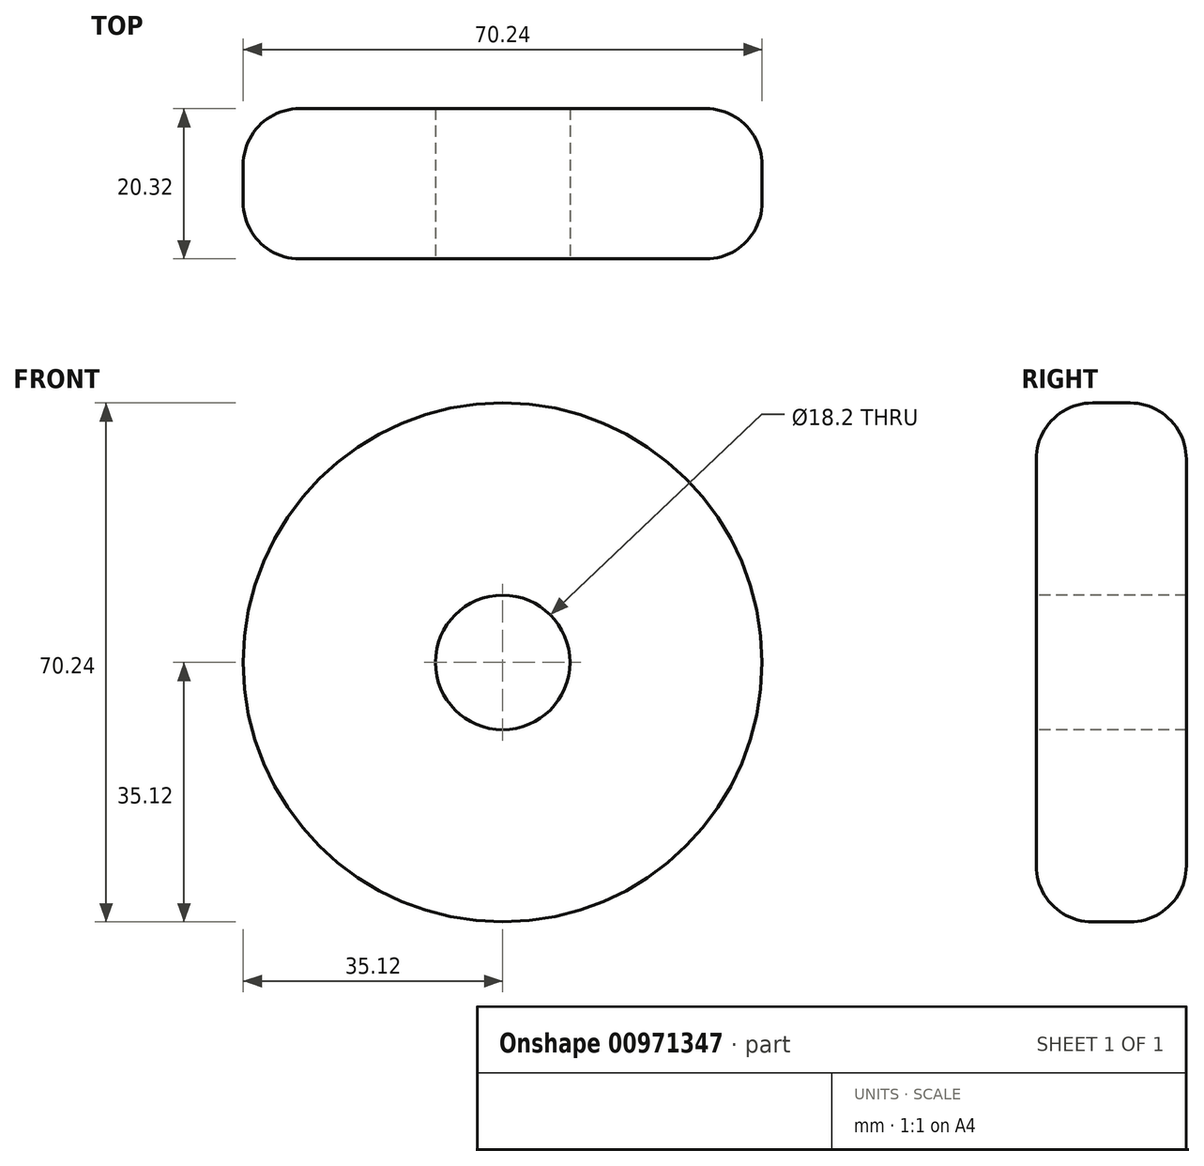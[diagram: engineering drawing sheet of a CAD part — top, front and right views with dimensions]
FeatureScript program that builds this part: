
annotation { "Feature Type Name" : "Feature", "Feature Type Description" : "" }
export const myFeature = defineFeature(function(context is Context, id is Id, definition is map)
    precondition{}
    {
        {
            var Q0;
            Q0=qCreatedBy(makeId("Front.planeOp"),FACE);
            var sketch = newSketch(context, id + "F0", { "sketchPlane" : qUnion([Q0])});
            skCircle(sketch, "E0", {"center": v(0, 0) * mm, "radius": 35.12 * mm});
            skSolve(sketch);
        }
        {
            var Q0;
            Q0=makeQuery(id+"F0.imprint","IMPRINT",FACE,{"disambiguationData":[TD([[makeQuery(id+"F0.imprint","IMPRINT",EDGE,{"derivedFrom":sQuery(id+"F0.wireOp",EDGE,"E0")}),1.0]])]});
            extrude(context, id + "F1", {"entities" : qUnion([Q0]), "depth" : 20.32 * mm, "offsetDistance" : 25.4 * mm});
        }
        {
            var Q0;
            Q0=makeQuery(id+"F1.opExtrude","CAP_FACE",FACE,{"disambiguationData":[OSD([sQuery(id+"F0.wireOp",EDGE,"E0")])],"isStart":false});
            var sketch = newSketch(context, id + "F2", { "sketchPlane" : qUnion([Q0])});
            skCircle(sketch, "E1", {"center": v(0, 0) * mm, "radius": 9.1 * mm});
            skSolve(sketch);
        }
        {
            var Q0;
            Q0=makeQuery(id+"F2.imprint","IMPRINT",FACE,{"disambiguationData":[TD([[makeQuery(id+"F2.imprint","IMPRINT",EDGE,{"derivedFrom":sQuery(id+"F2.wireOp",EDGE,"E1")}),1.0]])]});
            extrude(context, id + "F3", {"entities" : qUnion([Q0]), "operationType" : NewBodyOperationType.REMOVE, "oppositeDirection" : true, "depth" : 20.32 * mm, "offsetDistance" : 25.4 * mm});
        }
        {
            var Q0;
            Q0=makeQuery(id+"F1.opExtrude","CAP_EDGE",EDGE,{"disambiguationData":[OSD([sQuery(id+"F0.wireOp",EDGE,"E0")])],"isStart":true});
            var Q1;
            Q1=makeQuery(id+"F1.opExtrude","CAP_EDGE",EDGE,{"disambiguationData":[OSD([sQuery(id+"F0.wireOp",EDGE,"E0")])],"isStart":false});
            var Q2;
            Q2=makeQuery(id+"F3.boolean.opBoolean","COPY",EDGE,{"derivedFrom":makeQuery(id+"F3.opExtrude","CAP_EDGE",EDGE,{"disambiguationData":[OSD([sQuery(id+"F2.wireOp",EDGE,"E1")])],"isStart":true})});
            var Q3;
            Q3=makeQuery(id+"F3.boolean.opBoolean","COPY",EDGE,{"derivedFrom":makeQuery(id+"F3.opExtrude","CAP_EDGE",EDGE,{"disambiguationData":[OSD([sQuery(id+"F2.wireOp",EDGE,"E1")])],"isStart":false})});
            fillet(context, id + "F4", {"entities" : qUnion([Q0, Q1, Q2, Q3]), "radius" : 7.62 * mm, "tangentPropagation" : true, "allowEdgeOverflow" : false});
        }
    });
